# Revit family: Bottle_Filling_Station_Bi-Level-Elkay-VRCTLR8WSK
name_source: partatom
category: Plumbing Fixtures
units: mm (PartAtom-declared; Revit-internal decimal feet)

## family parameters
Always vertical = Yes
Cut with Voids When Loaded = No
Maintain Annotation Orientation = No
OmniClass Number = 23.65.70.14.11
OmniClass Title = Drinking Fountains/Coolers
Part Type = Normal
Room Calculation Point = No
Round Connector Dimension = Use Diameter
Shared = No
Work Plane-Based = No

## types (1)
- VRCTLR8WSK (Bottle Filling Station Bi-Level Reverse Vandal-Resistant )
    Activation Method = Electronic Bottle Filler Sensor With Mechanical Front Bubbler Button
    Approx. Shipping Weight (lbs) = 118
    Assembly Code = D2010800
    CW Connection = No
    CWFU = 0
    Chilling Capacity (GPH) = 8
    Connector Outlet B = 1.5 "
    Connector Supply A = 0.375 "
    Current = 0 A
    Default Elevation = 0 "
    Description = ezH2O® Vandal-Resistant Bottle Filling Station & Bi-Level Reverse Cooler Non-Filtered Refrigerated Stainless
    Dimensions (L x W x H) = 36 1/8 inch x 18 5/8 inch x 38 13/16 inch
    Floor to waste outlet = 18.75 "
    Floor to water supply loaction = 31.688 "
    HW Connection = No
    HWFU = 0
    Inlet Connection Size (inch) = 0.375 "
    Installation Location = Indoor + Outdoor
    Main Material = Elkay-Stainless Steel
    Manufacturer = Elkay Manufacturer Company
    Manufacturer Brand = Elkay (by Zurn Elkay Water Solutions)
    Model = VRCTLR8WSK
    Mounting Type = Wall Mount (On Wall)
    Number of Poles = 1
    Outlet Connection Size (inch) = 1.5 "
    Power Factor = 1
    Product Documentation Link = https://www.elkayfiles.com
    Product Installation Sheet URL = https://www.elkayfiles.com
    Product Page URL = https://www.elkay.com
    Product Weight (lbs) = 99
    Product data URL = https://www.bimobject.com
    Repair Parts URL = https://www.elkayfiles.com
    URL = https://www.elkay.com
    Voltage = 115 V
    WFU = 0
    Waste Connection = No

## geometry (parser evidence)
native form markers: Sweep x10
no freeform markers — native parametric forms only
